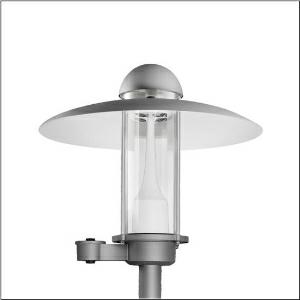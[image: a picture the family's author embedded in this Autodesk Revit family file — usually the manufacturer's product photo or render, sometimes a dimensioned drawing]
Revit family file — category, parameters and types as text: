
# Revit family: city-light_elegance___st1_2a_5xa5263es14h000032_75a3
name_source: partatom
category: Lighting Fixtures
units: mm (PartAtom-declared; Revit-internal decimal feet)

## family parameters
Cut with Voids When Loaded = No
Host = Face
Light Source = No
Part Type = Normal
Room Calculation Point = No
Round Connector Dimension = Use Diameter
Shared = No

## types (1)
- --- (1 x LED, 1470 lm, 14.2 W, 3000K)
    Apparent Load = 14 VA
    CIE Flux Codes = 22 62 94 98 100
    Color Rendering = 80
    Color Temperature = 3000K
    Default Elevation = 1800 mm
    Description = City-Light Elegance, mast luminaire, Module 540 Plus, primary light control with 3 zone facetted reflector, of plastic, silver coated, highly specular, structured, primary optical cover: cover, of PMMA, transparent, light distribution: ST1.2a, light emission: direct distribution, primary light characteristic: asymmetric, installation type: post-top, LED, High Power LED, rated luminous flux: 1.470lm, luminous efficacy: 104lm/W, light colour: 730, colour temperature: 3000K, control gear: ECG Smart Interface, control: overheat protection, digital communication interface, time-dependent luminous flux control, flexible luminous flux parameterisation, presetting dimming logarithmic, with terminal, 6-pole, max. 2.5mm², mains connection: 220..240V, AC, 50/60Hz, start of lifetime: 14W, end of lifetime: 15W, reduction: 8W, luminaire housing, upper part, of aluminium, coated, Siteco® metallic grey (DB 702S), diameter: 750mm, height: 675mm, spigot size: d x l = 76 x 70mm (post-top) | with reducer (optional accessory) 60 x 70mm, post-top mast mounting element, of diecast aluminium, coated, Siteco® metallic grey (DB 702S), Module 540 Plus, traffic white (RAL 9016), protection rating (complete): IP65, insulation class (complete): insulation class II (safety insulation), certification: CE, ENEC, VDE, packaging unit: 1 piece

Light Distribution: ST1.2a
    Height = 675 mm
    Lamp = 1 x LED
    Lamp Light Flux = 1470 lm
    Lamp Power = 14.2 W
    Lamp count = 1
    Length = 750 mm
    Luminous efficacy = 104 lm/W
    Manufacturer = Siteco
    ModVariant = No
    Model = 5XA5263ES14H000032
    Number of Poles = 1
    OnlyDefault = Yes
    Power Factor = 1
    Product Name = City-Light Elegance | ST1.2a
    Product group = mast luminaire | pylon top
    ProductGroupID = 6100
    Protection Class = Protection class II
    Protection Degree = IP 65
    RLX_Detail_Level = 1
    RlxData = <blob elided: 72549 chars, md5=832ce8c8>
    Socket = socket
    Standby Power = 0 W
    System Light Flux = 1470 lm
    System Power = 14 W
    Type Comments = factory setting: luminous flux: 100 % | dim-lin: 254 | 516 mA
    Type Image = l_1005991.jpg
    URL = http://relux.com
    VarID = @adj_121793
    Voltage = 0 V
    Weight = 0.00 kg
    Width = 0 mm  [stored 0 ft]

note: [stored X ft] marks values corroborated as IEEE doubles in the binary element streams (Revit-internal decimal feet)

## geometry (parser evidence)
native form markers: Blend x4, Sweep x12
no freeform markers — native parametric forms only
